# Revit family: PB_FIRE_FE
name_source: partatom
category: Fire Alarm Devices
units: mm (PartAtom-declared; Revit-internal decimal feet)

## family parameters
Always vertical = Yes
Cut with Voids When Loaded = No
Maintain Annotation Orientation = Yes
Part Type = Normal
Room Calculation Point = No
Round Connector Dimension = Use Diameter
Shared = No
Work Plane-Based = Yes

## types (5) — shared parameters
POA_Kiosk Extinguisher Body = POA_Kiosk Extinguisher Body Metal Red
POA_Kiosk Extinguisher Brand = POA_Kiosk Extinguisher Brand White
POA_Kiosk Extinguisher Handle = POA_Kiosk Extinguisher Component Metal Black
POA_Kiosk Extinguisher Rubber tube = POA_Kiosk Extinguisher Rubber tube Latex Black
POA_Kiosk Extinguisher Safety = POA_Kiosk Extinguisher Safety Metal Silver
POA_Kiosk Extinguisher Spray = POA_Kiosk Extinguisher Spray White
POA_Kiosk Extinguisher component = POA_Kiosk Extinguisher Component Metal Goal
Type Image = <None>
zero-valued in all types: Default Elevation

## per-type parameters (varying)
| type | CO2 | DC | Model | PB_ME_Type Mark |
| 5 kg Carbon Dioxide | No | Yes | T378A FPS | DC |
| 2 kg Carbon Dioxide | Yes | No |  | CO2 |
| 9 Litre Foam | Yes | Yes | T378A FPS | F |
| 4 kg ABC Dry Powder | No | Yes | T378A FPS | DC |
| 2 kg ABC Dry Powder | No | Yes |  | DC |

## geometry (parser evidence)
native form markers: Sweep x8
no freeform markers — native parametric forms only
